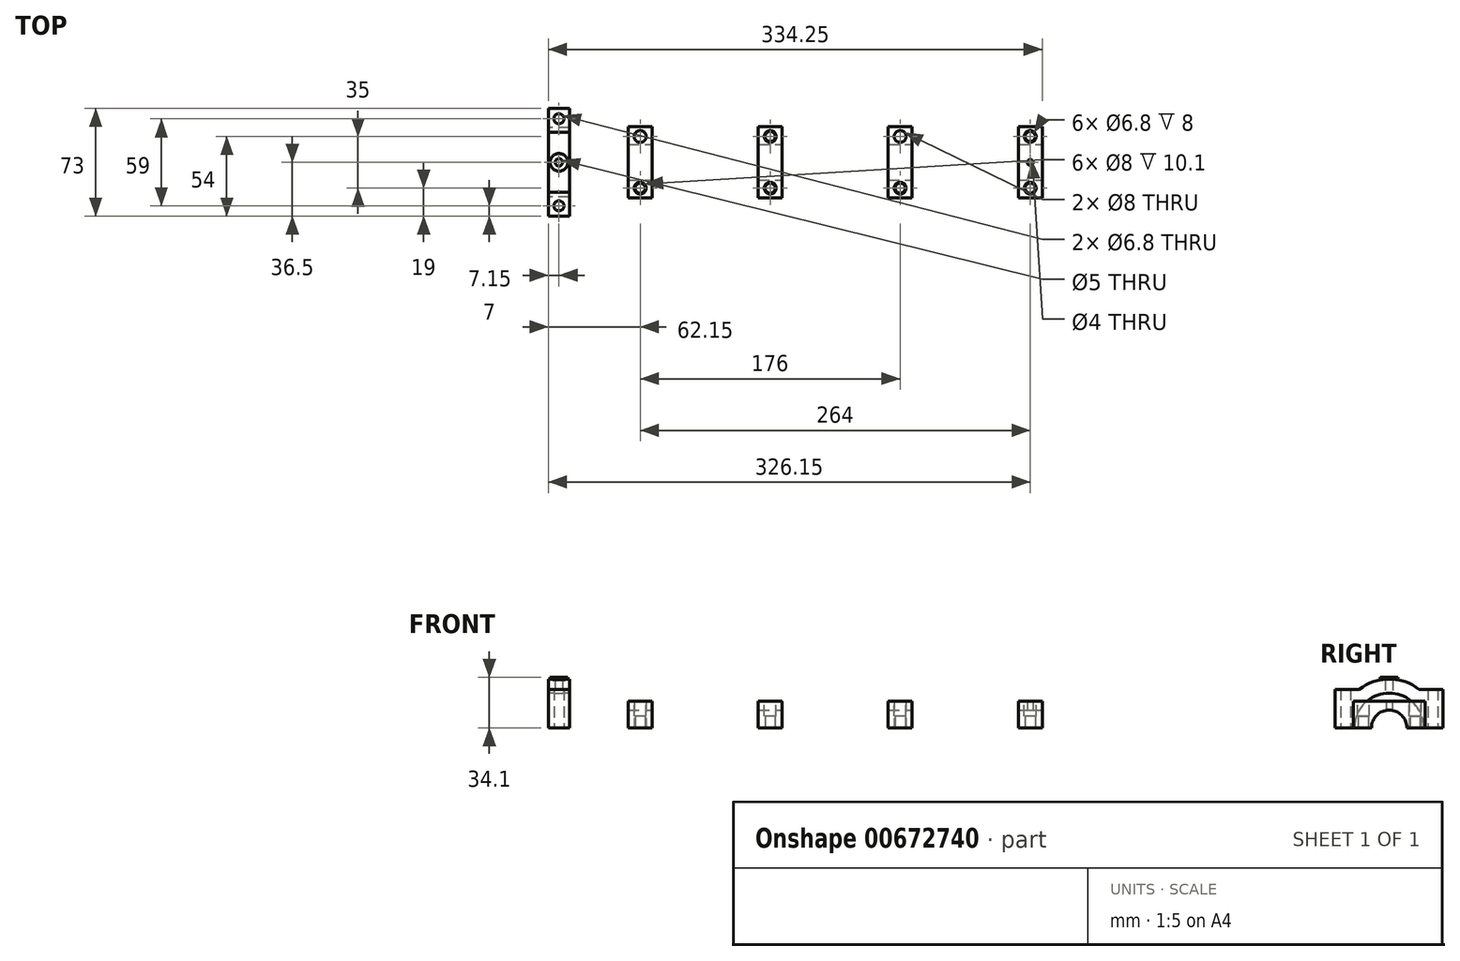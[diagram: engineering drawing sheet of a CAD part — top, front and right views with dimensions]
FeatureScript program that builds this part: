
annotation { "Feature Type Name" : "Feature", "Feature Type Description" : "" }
export const myFeature = defineFeature(function(context is Context, id is Id, definition is map)
    precondition{}
    {
        {
            var Q0;
            Q0=qCreatedBy(makeId("Top.planeOp"),FACE);
            var sketch = newSketch(context, id + "F0", { "sketchPlane" : qUnion([Q0])});
            skCircle(sketch, "E0", {"center": v(0, 0) * mm, "radius": 3.4 * mm});
            skCircle(sketch, "E1", {"center": v(55, -12) * mm, "radius": 4 * mm});
            skCircle(sketch, "E2", {"center": v(143, -12) * mm, "radius": 3.4 * mm});
            skCircle(sketch, "E3", {"center": v(319, -12) * mm, "radius": 3.4 * mm});
            skCircle(sketch, "E4", {"center": v(231, -12) * mm, "radius": 4 * mm});
            skCircle(sketch, "E5", {"center": v(231, -47) * mm, "radius": 3.4 * mm});
            skCircle(sketch, "E6", {"center": v(319, -47) * mm, "radius": 3.4 * mm});
            skCircle(sketch, "E7", {"center": v(143, -47) * mm, "radius": 3.4 * mm});
            skCircle(sketch, "E8", {"center": v(55, -47) * mm, "radius": 3.4 * mm});
            skCircle(sketch, "E9", {"center": v(0, -59) * mm, "radius": 3.4 * mm});
            skLineSegment(sketch, "E10", {"start": v(0, -29.5) * mm, "end": v(197.22, -29.5) * mm, "construction": true});
            skLineSegment(sketch, "E11", {"start": v(0, 0) * mm, "end": v(0, -59) * mm, "construction": true});
            skLineSegment(sketch, "E12", {"start": v(55, -12) * mm, "end": v(55, -47) * mm, "construction": true});
            skPoint(sketch, "E13", {"position": v(55, -29.5) * mm});
            skCircle(sketch, "E14", {"center": v(55, -12) * mm, "radius": 3.4 * mm});
            skCircle(sketch, "E15", {"center": v(231, -12) * mm, "radius": 3.4 * mm});
            skCircle(sketch, "E16", {"center": v(0, -29.5) * mm, "radius": 2.5 * mm});
            skCircle(sketch, "E17", {"center": v(27.5, -22) * mm, "radius": 3 * mm});
            skCircle(sketch, "E18", {"center": v(162.5, -22) * mm, "radius": 3 * mm});
            skCircle(sketch, "E19", {"center": v(298.5, -22) * mm, "radius": 3 * mm});
            skCircle(sketch, "E20", {"center": v(319, -29.5) * mm, "radius": 2 * mm});
            skLineSegment(sketch, "E21", {"start": v(55, 31.97) * mm, "end": v(55, -82.69) * mm, "construction": true});
            skLineSegment(sketch, "E22", {"start": v(143, 34.32) * mm, "end": v(143, -83.86) * mm, "construction": true});
            skLineSegment(sketch, "E23", {"start": v(231, 33.85) * mm, "end": v(231, -87.86) * mm, "construction": true});
            skLineSegment(sketch, "E24", {"start": v(319, 30.8) * mm, "end": v(319, -87.62) * mm, "construction": true});
            skLineSegment(sketch, "E25", {"start": v(0, 34.32) * mm, "end": v(0, -85.27) * mm, "construction": true});
            skSolve(sketch);
        }
        {
            var Q0;
            Q0=qCreatedBy(makeId("Top.planeOp"),FACE);
            var sketch = newSketch(context, id + "F1", { "sketchPlane" : qUnion([Q0])});
            skLineSegment(sketch, "E26", {"start": v(-7.15, 7) * mm, "end": v(-7.15, -66) * mm});
            skPoint(sketch, "E27", {"position": v(-7.15, -29.5) * mm});
            skLineSegment(sketch, "E28", {"start": v(-7.15, 7) * mm, "end": v(7.15, 7) * mm});
            skPoint(sketch, "E29", {"position": v(0, 7) * mm});
            skLineSegment(sketch, "E30", {"start": v(-7.15, -66) * mm, "end": v(7.15, -66) * mm});
            skLineSegment(sketch, "E31", {"start": v(7.15, -66) * mm, "end": v(7.15, -53.75) * mm});
            skLineSegment(sketch, "E32", {"start": v(7.15, -53.75) * mm, "end": v(327.1, -53.75) * mm});
            skLineSegment(sketch, "E33", {"start": v(327.1, -53.75) * mm, "end": v(327.1, -5.25) * mm});
            skLineSegment(sketch, "E34", {"start": v(327.1, -5.25) * mm, "end": v(7.15, -5.25) * mm});
            skLineSegment(sketch, "E35", {"start": v(7.15, -5.25) * mm, "end": v(7.15, 7) * mm});
            skPoint(sketch, "E36", {"position": v(327.1, -29.5) * mm});
            skSolve(sketch);
        }
        {
            var Q0;
            Q0 = qSketchRegion(id + "F1", true);
            extrude(context, id + "F2", {"entities" : qUnion([Q0]), "depth" : 39.1 * mm, "offsetDistance" : 25 * mm});
        }
        {
            var Q0;
            Q0=makeQuery(id+"F0.imprint","IMPRINT",FACE,{"disambiguationData":[TD([[makeQuery(id+"F0.imprint","IMPRINT",EDGE,{"derivedFrom":sQuery(id+"F0.wireOp",EDGE,"E1")}),1.0]])]});
            var Q1;
            Q1=makeQuery(id+"F0.imprint","IMPRINT",FACE,{"disambiguationData":[TD([[makeQuery(id+"F0.imprint","IMPRINT",EDGE,{"derivedFrom":sQuery(id+"F0.wireOp",EDGE,"E4")}),1.0]])]});
            extrude(context, id + "F3", {"entities" : qUnion([Q0, Q1]), "operationType" : NewBodyOperationType.REMOVE, "depth" : 11 * mm, "offsetDistance" : 25 * mm});
        }
        {
            var Q0;
            Q0=makeQuery(id+"F2.opExtrude","SWEPT_FACE",FACE,{"disambiguationData":[OSD([sQuery(id+"F1.wireOp",EDGE,"E33")])]});
            var sketch = newSketch(context, id + "F4", { "sketchPlane" : qUnion([Q0])});
            skCircle(sketch, "E37", {"center": v(-29.5, 0) * mm, "radius": 12 * mm});
            skSolve(sketch);
        }
        {
            var Q0;
            Q0 = qSketchRegion(id + "F4", true);
            var Q1;
            Q1=makeQuery(id+"F2.opExtrude","SWEPT_FACE",FACE,{"disambiguationData":[OSD([sQuery(id+"F1.wireOp",EDGE,"E26")])]});
            extrude(context, id + "F5", {"entities" : qUnion([Q0]), "operationType" : NewBodyOperationType.REMOVE, "endBound" : BoundingType.UP_TO_SURFACE, "oppositeDirection" : true, "depth" : 25 * mm, "endBoundEntityFace" : qUnion([Q1]), "offsetDistance" : 25 * mm});
        }
        {
            var Q0;
            Q0=makeQuery(id+"F2.opExtrude","SWEPT_FACE",FACE,{"disambiguationData":[OSD([sQuery(id+"F1.wireOp",EDGE,"E26")])]});
            var sketch = newSketch(context, id + "F6", { "sketchPlane" : qUnion([Q0])});
            skCircle(sketch, "E38", {"center": v(29.5, 0) * mm, "radius": 23.5 * mm});
            skSolve(sketch);
        }
        {
            var Q0;
            Q0 = qSketchRegion(id + "F6", true);
            var Q1;
            Q1=makeQuery(id+"F2.opExtrude","SWEPT_FACE",FACE,{"disambiguationData":[OSD([sQuery(id+"F1.wireOp",EDGE,"E31")])]});
            extrude(context, id + "F7", {"entities" : qUnion([Q0]), "operationType" : NewBodyOperationType.REMOVE, "oppositeDirection" : true, "depth" : 14.3 * mm, "endBoundEntityFace" : qUnion([Q1]), "offsetDistance" : 25 * mm});
        }
        {
            var Q0;
            Q0=qCreatedBy(makeId("Front.planeOp"),FACE);
            var sketch = newSketch(context, id + "F8", { "sketchPlane" : qUnion([Q0])});
            skLineSegment(sketch, "E39", {"start": v(7.15, 0) * mm, "end": v(7.15, 15.3) * mm});
            skLineSegment(sketch, "E40", {"start": v(7.15, 15.3) * mm, "end": v(46.85, 15.3) * mm});
            skLineSegment(sketch, "E41", {"start": v(46.85, 15.3) * mm, "end": v(46.85, 0) * mm});
            skLineSegment(sketch, "E42", {"start": v(46.85, 0) * mm, "end": v(63.15, 0) * mm});
            skLineSegment(sketch, "E43", {"start": v(63.15, 0) * mm, "end": v(63.15, 15.3) * mm});
            skLineSegment(sketch, "E44", {"start": v(63.15, 15.3) * mm, "end": v(134.85, 15.3) * mm});
            skLineSegment(sketch, "E45", {"start": v(134.85, 15.3) * mm, "end": v(134.85, 0) * mm});
            skLineSegment(sketch, "E46", {"start": v(134.85, 0) * mm, "end": v(151.15, 0) * mm});
            skLineSegment(sketch, "E47", {"start": v(151.15, 0) * mm, "end": v(151.15, 15.3) * mm});
            skLineSegment(sketch, "E48", {"start": v(151.15, 15.3) * mm, "end": v(222.85, 15.3) * mm});
            skLineSegment(sketch, "E49", {"start": v(222.85, 15.3) * mm, "end": v(222.85, 0) * mm});
            skLineSegment(sketch, "E50", {"start": v(222.85, 0) * mm, "end": v(239.15, 0) * mm});
            skLineSegment(sketch, "E51", {"start": v(239.15, 0) * mm, "end": v(239.15, 15.3) * mm});
            skLineSegment(sketch, "E52", {"start": v(239.15, 15.3) * mm, "end": v(310.9, 15.3) * mm});
            skLineSegment(sketch, "E53", {"start": v(310.9, 15.3) * mm, "end": v(310.9, 0) * mm});
            skLineSegment(sketch, "E54", {"start": v(310.9, 0) * mm, "end": v(327.1, 0) * mm});
            skLineSegment(sketch, "E55", {"start": v(327.1, 0) * mm, "end": v(327.1, 15.3) * mm});
            skLineSegment(sketch, "E56", {"start": v(7.15, 0) * mm, "end": v(310.9, 0) * mm});
            skPoint(sketch, "E57", {"position": v(55, 0) * mm});
            skPoint(sketch, "E58", {"position": v(143, 0) * mm});
            skPoint(sketch, "E59", {"position": v(231, 0) * mm});
            skPoint(sketch, "E60", {"position": v(319, 0) * mm});
            skSolve(sketch);
        }
        {
            var Q0;
            {var subQ0=sQuery(id+"F8.wireOp",EDGE,"E39");Q0=makeQuery(id+"F8.imprint","IMPRINT",FACE,{"disambiguationData":[TD([[makeQuery(id+"F8.imprint","IMPRINT",EDGE,{"derivedFrom":subQ0}),-1.0]])]});}
            var Q1;
            {var subQ0=sQuery(id+"F8.wireOp",EDGE,"E43");Q1=makeQuery(id+"F8.imprint","IMPRINT",FACE,{"disambiguationData":[TD([[makeQuery(id+"F8.imprint","IMPRINT",EDGE,{"derivedFrom":subQ0}),-1.0]])]});}
            var Q2;
            {var subQ0=sQuery(id+"F8.wireOp",EDGE,"E47");Q2=makeQuery(id+"F8.imprint","IMPRINT",FACE,{"disambiguationData":[TD([[makeQuery(id+"F8.imprint","IMPRINT",EDGE,{"derivedFrom":subQ0}),-1.0]])]});}
            var Q3;
            {var subQ0=sQuery(id+"F8.wireOp",EDGE,"E51");Q3=makeQuery(id+"F8.imprint","IMPRINT",FACE,{"disambiguationData":[TD([[makeQuery(id+"F8.imprint","IMPRINT",EDGE,{"derivedFrom":subQ0}),-1.0]])]});}
            var Q4;
            Q4=makeQuery(id+"F2.opExtrude","SWEPT_FACE",FACE,{"disambiguationData":[OSD([sQuery(id+"F1.wireOp",EDGE,"E32")])]});
            extrude(context, id + "F9", {"entities" : qUnion([Q0, Q1, Q2, Q3]), "operationType" : NewBodyOperationType.REMOVE, "endBound" : BoundingType.UP_TO_SURFACE, "depth" : 25 * mm, "endBoundEntityFace" : qUnion([Q4]), "offsetDistance" : 25 * mm});
        }
        {
            var Q0;
            Q0=makeQuery(id+"F9.boolean.opBoolean","MERGE",FACE,{"derivedFrom":[makeQuery(id+"F2.opExtrude","SWEPT_FACE",FACE,{"disambiguationData":[OSD([sQuery(id+"F1.wireOp",EDGE,"E31")])]}),makeQuery(id+"F9.opExtrude","SWEPT_FACE",FACE,{"disambiguationData":[OSD([sQuery(id+"F8.wireOp",EDGE,"E39")])]})]});
            cPlane(context, id + "F10", {"entities" : qUnion([Q0]), "cplaneType" : CPlaneType.OFFSET, "offset" : 0 * mm, "width" : 150 * mm, "height" : 150 * mm});
        }
        {
            var Q0;
            Q0=makeQuery(id+"F9.boolean.opBoolean","COPY",FACE,{"derivedFrom":makeQuery(id+"F9.opExtrude","SWEPT_FACE",FACE,{"disambiguationData":[OSD([sQuery(id+"F8.wireOp",EDGE,"E43")])]})});
            cPlane(context, id + "F11", {"entities" : qUnion([Q0]), "cplaneType" : CPlaneType.OFFSET, "offset" : 0 * mm, "width" : 150 * mm, "height" : 150 * mm});
        }
        {
            var Q0;
            Q0=makeQuery(id+"F9.boolean.opBoolean","COPY",FACE,{"derivedFrom":makeQuery(id+"F9.opExtrude","SWEPT_FACE",FACE,{"disambiguationData":[OSD([sQuery(id+"F8.wireOp",EDGE,"E47")])]})});
            cPlane(context, id + "F12", {"entities" : qUnion([Q0]), "cplaneType" : CPlaneType.OFFSET, "offset" : 0 * mm, "width" : 150 * mm, "height" : 150 * mm});
        }
        {
            var Q0;
            Q0=makeQuery(id+"F9.boolean.opBoolean","COPY",FACE,{"derivedFrom":makeQuery(id+"F9.opExtrude","SWEPT_FACE",FACE,{"disambiguationData":[OSD([sQuery(id+"F8.wireOp",EDGE,"E51")])]})});
            cPlane(context, id + "F13", {"entities" : qUnion([Q0]), "cplaneType" : CPlaneType.OFFSET, "offset" : 0 * mm, "width" : 150 * mm, "height" : 150 * mm});
        }
        {
            var Q0;
            Q0=makeQuery(id+"F2.opExtrude","CAP_FACE",FACE,{"disambiguationData":[OSD([sQuery(id+"F1.wireOp",EDGE,"E26"),sQuery(id+"F1.wireOp",EDGE,"E28"),sQuery(id+"F1.wireOp",EDGE,"E30"),sQuery(id+"F1.wireOp",EDGE,"E31"),sQuery(id+"F1.wireOp",EDGE,"E32"),sQuery(id+"F1.wireOp",EDGE,"E33"),sQuery(id+"F1.wireOp",EDGE,"E34"),sQuery(id+"F1.wireOp",EDGE,"E35")])],"isStart":false});
            cPlane(context, id + "F14", {"entities" : qUnion([Q0]), "cplaneType" : CPlaneType.OFFSET, "offset" : 0 * mm, "width" : 150 * mm, "height" : 150 * mm});
        }
        {
            var Q0;
            Q0=qCreatedBy(id+"F14.planeOp",FACE);
            var sketch = newSketch(context, id + "F15", { "sketchPlane" : qUnion([Q0])});
            skCircle(sketch, "E61", {"center": v(298.5, -22) * mm, "radius": 6.5 * mm});
            skCircle(sketch, "E62", {"center": v(162.5, -22) * mm, "radius": 6.5 * mm});
            skCircle(sketch, "E63", {"center": v(27.5, -22) * mm, "radius": 6.5 * mm});
            skCircle(sketch, "E64", {"center": v(0, -29.5) * mm, "radius": 6 * mm});
            skSolve(sketch);
        }
        {
            var Q0;
            Q0=qCreatedBy(id+"F10.planeOp",FACE);
            var sketch = newSketch(context, id + "F16", { "sketchPlane" : qUnion([Q0])});
            skCircle(sketch, "E65", {"center": v(-29.5, 0) * mm, "radius": 24.75 * mm});
            skSolve(sketch);
        }
        {
            var Q0;
            Q0=qCreatedBy(id+"F11.planeOp",FACE);
            var sketch = newSketch(context, id + "F17", { "sketchPlane" : qUnion([Q0])});
            skCircle(sketch, "E66", {"center": v(-29.5, 0) * mm, "radius": 25 * mm});
            skSolve(sketch);
        }
        {
            var Q0;
            Q0=qCreatedBy(id+"F12.planeOp",FACE);
            var sketch = newSketch(context, id + "F18", { "sketchPlane" : qUnion([Q0])});
            skCircle(sketch, "E67", {"center": v(-29.5, 0) * mm, "radius": 25 * mm});
            skSolve(sketch);
        }
        {
            var Q0;
            Q0=qCreatedBy(id+"F13.planeOp",FACE);
            var sketch = newSketch(context, id + "F19", { "sketchPlane" : qUnion([Q0])});
            skCircle(sketch, "E68", {"center": v(-29.5, 0) * mm, "radius": 25 * mm});
            skSolve(sketch);
        }
        {
            var Q0;
            Q0=makeQuery(id+"F2.opExtrude","SWEPT_FACE",FACE,{"disambiguationData":[OSD([sQuery(id+"F1.wireOp",EDGE,"E26")])]});
            cPlane(context, id + "F20", {"entities" : qUnion([Q0]), "cplaneType" : CPlaneType.OFFSET, "offset" : 0 * mm, "width" : 150 * mm, "height" : 150 * mm});
        }
        {
            var Q0;
            Q0=qCreatedBy(id+"F20.planeOp",FACE);
            var sketch = newSketch(context, id + "F21", { "sketchPlane" : qUnion([Q0])});
            skArc(sketch, "E69", {"start": v(49.82, 26) * mm, "mid": v(29.5, 33) * mm, "end": v(9.18, 26) * mm});
            skLineSegment(sketch, "E70", {"start": v(-7, 26) * mm, "end": v(9.18, 26) * mm});
            skLineSegment(sketch, "E71", {"start": v(49.82, 26) * mm, "end": v(66, 26) * mm});
            skLineSegment(sketch, "E72", {"start": v(-7, 26) * mm, "end": v(-7, 39.1) * mm});
            skLineSegment(sketch, "E73", {"start": v(-7, 39.1) * mm, "end": v(66, 39.1) * mm});
            skLineSegment(sketch, "E74", {"start": v(66, 39.1) * mm, "end": v(66, 26) * mm});
            skSolve(sketch);
        }
        {
            var Q0;
            Q0 = qSketchRegion(id + "F21", true);
            var Q1;
            {var subQ0=sQuery(id+"F16.wireOp",EDGE,"E65");var subQ1=sQuery(id+"F8.wireOp",EDGE,"E39");var subQ2=sQuery(id+"F1.wireOp",EDGE,"E35");var subQ3=sQuery(id+"F1.wireOp",EDGE,"E31");var subQ4=makeQuery(id+"F9.opExtrude","SWEPT_FACE",FACE,{"disambiguationData":[OSD([subQ1])]});Q1=makeQuery(id+"F31.boolean.opBoolean","MERGE",FACE,{"derivedFrom":[makeQuery(id+"F23.boolean.opBoolean","MERGE",FACE,{"derivedFrom":[makeQuery(id+"F9.boolean.opBoolean","MERGE",FACE,{"derivedFrom":[makeQuery(id+"F2.opExtrude","SWEPT_FACE",FACE,{"disambiguationData":[OSD([subQ3])]}),subQ4]}),makeQuery(id+"F9.boolean.opBoolean","MERGE",FACE,{"derivedFrom":[makeQuery(id+"F2.opExtrude","SWEPT_FACE",FACE,{"disambiguationData":[OSD([subQ2])]}),subQ4]}),makeQuery(id+"F23.opExtrude","CAP_FACE",FACE,{"disambiguationData":[OSD([subQ0])],"isStart":true})]}),makeQuery(id+"F31.opExtrude","CAP_FACE",FACE,{"disambiguationData":[OSD([subQ3,subQ2,subQ1,subQ0])],"isStart":false})]});}
            extrude(context, id + "F22", {"entities" : qUnion([Q0]), "operationType" : NewBodyOperationType.REMOVE, "endBound" : BoundingType.UP_TO_SURFACE, "oppositeDirection" : true, "depth" : 25 * mm, "endBoundEntityFace" : qUnion([Q1]), "offsetDistance" : 25 * mm});
        }
        {
            var Q0;
            Q0=makeQuery(id+"F16.imprint","IMPRINT",FACE,{"disambiguationData":[TD([[makeQuery(id+"F16.imprint","IMPRINT",EDGE,{"derivedFrom":sQuery(id+"F16.wireOp",EDGE,"E65")}),1.0]])]});
            var Q1;
            Q1=makeQuery(id+"F9.boolean.opBoolean","COPY",FACE,{"derivedFrom":makeQuery(id+"F9.opExtrude","SWEPT_FACE",FACE,{"disambiguationData":[OSD([sQuery(id+"F8.wireOp",EDGE,"E41")])]})});
            extrude(context, id + "F23", {"entities" : qUnion([Q0]), "operationType" : NewBodyOperationType.REMOVE, "endBound" : BoundingType.UP_TO_SURFACE, "depth" : 25 * mm, "endBoundEntityFace" : qUnion([Q1]), "offsetDistance" : 25 * mm});
        }
        {
            var Q0;
            Q0=makeQuery(id+"F17.imprint","IMPRINT",FACE,{"disambiguationData":[TD([[makeQuery(id+"F17.imprint","IMPRINT",EDGE,{"derivedFrom":sQuery(id+"F17.wireOp",EDGE,"E66")}),1.0]])]});
            var Q1;
            Q1=makeQuery(id+"F9.boolean.opBoolean","COPY",FACE,{"derivedFrom":makeQuery(id+"F9.opExtrude","SWEPT_FACE",FACE,{"disambiguationData":[OSD([sQuery(id+"F8.wireOp",EDGE,"E45")])]})});
            extrude(context, id + "F24", {"entities" : qUnion([Q0]), "operationType" : NewBodyOperationType.REMOVE, "endBound" : BoundingType.UP_TO_SURFACE, "depth" : 25 * mm, "endBoundEntityFace" : qUnion([Q1]), "offsetDistance" : 25 * mm});
        }
        {
            var Q0;
            Q0=makeQuery(id+"F18.imprint","IMPRINT",FACE,{"disambiguationData":[TD([[makeQuery(id+"F18.imprint","IMPRINT",EDGE,{"derivedFrom":sQuery(id+"F18.wireOp",EDGE,"E67")}),1.0]])]});
            var Q1;
            Q1=makeQuery(id+"F9.boolean.opBoolean","COPY",FACE,{"derivedFrom":makeQuery(id+"F9.opExtrude","SWEPT_FACE",FACE,{"disambiguationData":[OSD([sQuery(id+"F8.wireOp",EDGE,"E49")])]})});
            extrude(context, id + "F25", {"entities" : qUnion([Q0]), "operationType" : NewBodyOperationType.REMOVE, "endBound" : BoundingType.UP_TO_SURFACE, "depth" : 25 * mm, "endBoundEntityFace" : qUnion([Q1]), "offsetDistance" : 25 * mm});
        }
        {
            var Q0;
            Q0=makeQuery(id+"F19.imprint","IMPRINT",FACE,{"disambiguationData":[TD([[makeQuery(id+"F19.imprint","IMPRINT",EDGE,{"derivedFrom":sQuery(id+"F19.wireOp",EDGE,"E68")}),1.0]])]});
            var Q1;
            Q1=makeQuery(id+"F9.boolean.opBoolean","COPY",FACE,{"derivedFrom":makeQuery(id+"F9.opExtrude","SWEPT_FACE",FACE,{"disambiguationData":[OSD([sQuery(id+"F8.wireOp",EDGE,"E53")])]})});
            extrude(context, id + "F26", {"entities" : qUnion([Q0]), "operationType" : NewBodyOperationType.REMOVE, "endBound" : BoundingType.UP_TO_SURFACE, "depth" : 25 * mm, "endBoundEntityFace" : qUnion([Q1]), "offsetDistance" : 25 * mm});
        }
        {
            var Q0;
            Q0=makeQuery(id+"F2.opExtrude","CAP_FACE",FACE,{"disambiguationData":[OSD([sQuery(id+"F1.wireOp",EDGE,"E26"),sQuery(id+"F1.wireOp",EDGE,"E28"),sQuery(id+"F1.wireOp",EDGE,"E30"),sQuery(id+"F1.wireOp",EDGE,"E31"),sQuery(id+"F1.wireOp",EDGE,"E32"),sQuery(id+"F1.wireOp",EDGE,"E33"),sQuery(id+"F1.wireOp",EDGE,"E34"),sQuery(id+"F1.wireOp",EDGE,"E35")])],"isStart":false});
            var sketch = newSketch(context, id + "F27", { "sketchPlane" : qUnion([Q0])});
            skArc(sketch, "E75", {"start": v(327.1, -47) * mm, "mid": v(319, -38.9) * mm, "end": v(310.9, -47) * mm});
            skLineSegment(sketch, "E76", {"start": v(310.9, -47) * mm, "end": v(310.9, -59) * mm});
            skLineSegment(sketch, "E77", {"start": v(310.9, -59) * mm, "end": v(327.1, -59) * mm});
            skLineSegment(sketch, "E78", {"start": v(327.1, -59) * mm, "end": v(327.1, -47) * mm});
            skArc(sketch, "E79", {"start": v(239.1, -47) * mm, "mid": v(231, -38.9) * mm, "end": v(222.9, -47) * mm});
            skLineSegment(sketch, "E80", {"start": v(222.9, -47) * mm, "end": v(222.9, -59) * mm});
            skLineSegment(sketch, "E81", {"start": v(222.9, -59) * mm, "end": v(239.1, -59) * mm});
            skLineSegment(sketch, "E82", {"start": v(239.1, -59) * mm, "end": v(239.1, -47) * mm});
            skArc(sketch, "E83", {"start": v(151.1, -47) * mm, "mid": v(143, -38.9) * mm, "end": v(134.9, -47) * mm});
            skLineSegment(sketch, "E84", {"start": v(134.9, -47) * mm, "end": v(134.9, -59) * mm});
            skLineSegment(sketch, "E85", {"start": v(134.9, -59) * mm, "end": v(151.1, -59) * mm});
            skLineSegment(sketch, "E86", {"start": v(151.1, -59) * mm, "end": v(151.1, -47) * mm});
            skArc(sketch, "E87", {"start": v(63.1, -47) * mm, "mid": v(55, -38.9) * mm, "end": v(46.9, -47) * mm});
            skLineSegment(sketch, "E88", {"start": v(46.9, -47) * mm, "end": v(46.9, -59) * mm});
            skLineSegment(sketch, "E89", {"start": v(46.9, -59) * mm, "end": v(63.1, -59) * mm});
            skLineSegment(sketch, "E90", {"start": v(63.1, -59) * mm, "end": v(63.1, -47) * mm});
            skLineSegment(sketch, "E91", {"start": v(-23.17, -29.5) * mm, "end": v(371.55, -29.5) * mm, "construction": true});
            skArc(sketch, "E92.MirrorC", {"start": v(327.1, -12) * mm, "mid": v(319, -20.1) * mm, "end": v(310.9, -12) * mm});
            skLineSegment(sketch, "E93.MirrorCS", {"start": v(63.1, 0) * mm, "end": v(63.1, -12) * mm});
            skLineSegment(sketch, "E94.MirrorCS", {"start": v(46.9, 0) * mm, "end": v(63.1, 0) * mm});
            skLineSegment(sketch, "E95.MirrorCS", {"start": v(46.9, -12) * mm, "end": v(46.9, 0) * mm});
            skLineSegment(sketch, "E96.MirrorCS", {"start": v(239.1, 0) * mm, "end": v(239.1, -12) * mm});
            skArc(sketch, "E97.MirrorC", {"start": v(63.1, -12) * mm, "mid": v(55, -20.1) * mm, "end": v(46.9, -12) * mm});
            skLineSegment(sketch, "E98.MirrorCS", {"start": v(151.1, 0) * mm, "end": v(151.1, -12) * mm});
            skArc(sketch, "E99.MirrorC", {"start": v(151.1, -12) * mm, "mid": v(143, -20.1) * mm, "end": v(134.9, -12) * mm});
            skLineSegment(sketch, "E100.MirrorCS", {"start": v(310.9, -12) * mm, "end": v(310.9, 0) * mm});
            skLineSegment(sketch, "E101.MirrorCS", {"start": v(134.9, -12) * mm, "end": v(134.9, 0) * mm});
            skLineSegment(sketch, "E102.MirrorCS", {"start": v(222.9, -12) * mm, "end": v(222.9, 0) * mm});
            skLineSegment(sketch, "E103.MirrorCS", {"start": v(222.9, 0) * mm, "end": v(239.1, 0) * mm});
            skArc(sketch, "E104.MirrorC", {"start": v(239.1, -12) * mm, "mid": v(231, -20.1) * mm, "end": v(222.9, -12) * mm});
            skLineSegment(sketch, "E105.MirrorCS", {"start": v(327.1, 0) * mm, "end": v(327.1, -12) * mm});
            skLineSegment(sketch, "E106.MirrorCS", {"start": v(134.9, 0) * mm, "end": v(151.1, 0) * mm});
            skLineSegment(sketch, "E107.MirrorCS", {"start": v(310.9, 0) * mm, "end": v(327.1, 0) * mm});
            skSolve(sketch);
        }
        {
            var Q0;
            {var subQ2=sQuery(id+"F27.wireOp",EDGE,"E87");Q0=makeQuery(id+"F27.imprint","IMPRINT",FACE,{"disambiguationData":[TD([[makeQuery(id+"F27.imprint","IMPRINT",EDGE,{"derivedFrom":subQ2}),1.0]])]});}
            var Q1;
            {var subQ1=sQuery(id+"F27.wireOp",EDGE,"E97.MirrorC");Q1=makeQuery(id+"F27.imprint","IMPRINT",FACE,{"disambiguationData":[TD([[makeQuery(id+"F27.imprint","IMPRINT",EDGE,{"derivedFrom":subQ1}),-1.0]])]});}
            var Q2;
            {var subQ1=sQuery(id+"F27.wireOp",EDGE,"E99.MirrorC");Q2=makeQuery(id+"F27.imprint","IMPRINT",FACE,{"disambiguationData":[TD([[makeQuery(id+"F27.imprint","IMPRINT",EDGE,{"derivedFrom":subQ1}),-1.0]])]});}
            var Q3;
            {var subQ2=sQuery(id+"F27.wireOp",EDGE,"E83");Q3=makeQuery(id+"F27.imprint","IMPRINT",FACE,{"disambiguationData":[TD([[makeQuery(id+"F27.imprint","IMPRINT",EDGE,{"derivedFrom":subQ2}),1.0]])]});}
            var Q4;
            {var subQ1=sQuery(id+"F27.wireOp",EDGE,"E104.MirrorC");Q4=makeQuery(id+"F27.imprint","IMPRINT",FACE,{"disambiguationData":[TD([[makeQuery(id+"F27.imprint","IMPRINT",EDGE,{"derivedFrom":subQ1}),-1.0]])]});}
            var Q5;
            {var subQ2=sQuery(id+"F27.wireOp",EDGE,"E79");Q5=makeQuery(id+"F27.imprint","IMPRINT",FACE,{"disambiguationData":[TD([[makeQuery(id+"F27.imprint","IMPRINT",EDGE,{"derivedFrom":subQ2}),1.0]])]});}
            var Q6;
            {var subQ4=sQuery(id+"F27.wireOp",EDGE,"E92.MirrorC");Q6=makeQuery(id+"F27.imprint","IMPRINT",FACE,{"disambiguationData":[TD([[makeQuery(id+"F27.imprint","IMPRINT",EDGE,{"derivedFrom":subQ4}),-1.0]])]});}
            var Q7;
            {var subQ7=sQuery(id+"F27.wireOp",EDGE,"E75");Q7=makeQuery(id+"F27.imprint","IMPRINT",FACE,{"disambiguationData":[TD([[makeQuery(id+"F27.imprint","IMPRINT",EDGE,{"derivedFrom":subQ7}),1.0]])]});}
            extrude(context, id + "F28", {"entities" : qUnion([Q0, Q1, Q2, Q3, Q4, Q5, Q6, Q7]), "operationType" : NewBodyOperationType.REMOVE, "oppositeDirection" : true, "depth" : 18 * mm, "offsetDistance" : 25 * mm});
        }
        {
            var Q0;
            Q0=makeQuery(id+"F2.opExtrude","SWEPT_FACE",FACE,{"disambiguationData":[OSD([sQuery(id+"F1.wireOp",EDGE,"E33")])]});
            cPlane(context, id + "F29", {"entities" : qUnion([Q0]), "cplaneType" : CPlaneType.OFFSET, "offset" : 0 * mm, "width" : 150 * mm, "height" : 150 * mm});
        }
        {
            var Q0;
            Q0=qCreatedBy(id+"F29.planeOp",FACE);
            var sketch = newSketch(context, id + "F30", { "sketchPlane" : qUnion([Q0])});
            skCircle(sketch, "E108", {"center": v(-29.5, 0) * mm, "radius": 30.8 * mm});
            skCircle(sketch, "E109", {"center": v(-29.5, 0) * mm, "radius": 50 * mm});
            skSolve(sketch);
        }
        {
            var Q0;
            Q0=makeQuery(id+"F30.imprint","IMPRINT",FACE,{"disambiguationData":[TD([[makeQuery(id+"F30.imprint","IMPRINT",EDGE,{"derivedFrom":sQuery(id+"F30.wireOp",EDGE,"E108")}),-1.0]])]});
            var Q1;
            {var subQ0=makeQuery(id+"F9.opExtrude","SWEPT_FACE",FACE,{"disambiguationData":[OSD([sQuery(id+"F8.wireOp",EDGE,"E39")])]});Q1=makeQuery(id+"F23.boolean.opBoolean","MERGE",FACE,{"derivedFrom":[makeQuery(id+"F9.boolean.opBoolean","MERGE",FACE,{"derivedFrom":[makeQuery(id+"F2.opExtrude","SWEPT_FACE",FACE,{"disambiguationData":[OSD([sQuery(id+"F1.wireOp",EDGE,"E31")])]}),subQ0]}),makeQuery(id+"F9.boolean.opBoolean","MERGE",FACE,{"derivedFrom":[makeQuery(id+"F2.opExtrude","SWEPT_FACE",FACE,{"disambiguationData":[OSD([sQuery(id+"F1.wireOp",EDGE,"E35")])]}),subQ0]}),makeQuery(id+"F23.opExtrude","CAP_FACE",FACE,{"disambiguationData":[OSD([sQuery(id+"F16.wireOp",EDGE,"E65")])],"isStart":true})]});}
            extrude(context, id + "F31", {"entities" : qUnion([Q0]), "operationType" : NewBodyOperationType.REMOVE, "endBound" : BoundingType.UP_TO_SURFACE, "oppositeDirection" : true, "depth" : 287.2 * mm, "endBoundEntityFace" : qUnion([Q1]), "offsetDistance" : 25 * mm});
        }
        {
            var Q0;
            Q0=makeQuery(id+"F15.imprint","IMPRINT",FACE,{"disambiguationData":[TD([[makeQuery(id+"F15.imprint","IMPRINT",EDGE,{"derivedFrom":sQuery(id+"F15.wireOp",EDGE,"E63")}),1.0]])]});
            var Q1;
            Q1=makeQuery(id+"F15.imprint","IMPRINT",FACE,{"disambiguationData":[TD([[makeQuery(id+"F15.imprint","IMPRINT",EDGE,{"derivedFrom":sQuery(id+"F15.wireOp",EDGE,"E62")}),1.0]])]});
            var Q2;
            Q2=makeQuery(id+"F15.imprint","IMPRINT",FACE,{"disambiguationData":[TD([[makeQuery(id+"F15.imprint","IMPRINT",EDGE,{"derivedFrom":sQuery(id+"F15.wireOp",EDGE,"E61")}),1.0]])]});
            var Q3;
            Q3=makeQuery(id+"F15.imprint","IMPRINT",FACE,{"disambiguationData":[TD([[makeQuery(id+"F15.imprint","IMPRINT",EDGE,{"derivedFrom":sQuery(id+"F15.wireOp",EDGE,"E64")}),1.0]])]});
            var Q4;
            Q4=makeQuery(id+"F31.boolean.opBoolean","COPY",FACE,{"derivedFrom":makeQuery(id+"F31.opExtrude","SWEPT_FACE",FACE,{"disambiguationData":[OSD([sQuery(id+"F30.wireOp",EDGE,"E108")])]})});
            extrude(context, id + "F32", {"entities" : qUnion([Q0, Q1, Q2, Q3]), "operationType" : NewBodyOperationType.ADD, "endBound" : BoundingType.UP_TO_SURFACE, "oppositeDirection" : true, "depth" : 25 * mm, "endBoundEntityFace" : qUnion([Q4]), "offsetDistance" : 25 * mm});
        }
        {
            var Q0;
            Q0=makeQuery(id+"F0.imprint","IMPRINT",FACE,{"disambiguationData":[TD([[makeQuery(id+"F0.imprint","IMPRINT",EDGE,{"derivedFrom":sQuery(id+"F0.wireOp",EDGE,"E0")}),1.0]])]});
            var Q1;
            Q1=makeQuery(id+"F0.imprint","IMPRINT",FACE,{"disambiguationData":[TD([[makeQuery(id+"F0.imprint","IMPRINT",EDGE,{"derivedFrom":sQuery(id+"F0.wireOp",EDGE,"E2")}),1.0]])]});
            var Q2;
            Q2=makeQuery(id+"F0.imprint","IMPRINT",FACE,{"disambiguationData":[TD([[makeQuery(id+"F0.imprint","IMPRINT",EDGE,{"derivedFrom":sQuery(id+"F0.wireOp",EDGE,"E3")}),1.0]])]});
            var Q3;
            Q3=makeQuery(id+"F0.imprint","IMPRINT",FACE,{"disambiguationData":[TD([[makeQuery(id+"F0.imprint","IMPRINT",EDGE,{"derivedFrom":sQuery(id+"F0.wireOp",EDGE,"E5")}),1.0]])]});
            var Q4;
            Q4=makeQuery(id+"F0.imprint","IMPRINT",FACE,{"disambiguationData":[TD([[makeQuery(id+"F0.imprint","IMPRINT",EDGE,{"derivedFrom":sQuery(id+"F0.wireOp",EDGE,"E6")}),1.0]])]});
            var Q5;
            Q5=makeQuery(id+"F0.imprint","IMPRINT",FACE,{"disambiguationData":[TD([[makeQuery(id+"F0.imprint","IMPRINT",EDGE,{"derivedFrom":sQuery(id+"F0.wireOp",EDGE,"E7")}),1.0]])]});
            var Q6;
            Q6=makeQuery(id+"F0.imprint","IMPRINT",FACE,{"disambiguationData":[TD([[makeQuery(id+"F0.imprint","IMPRINT",EDGE,{"derivedFrom":sQuery(id+"F0.wireOp",EDGE,"E8")}),1.0]])]});
            var Q7;
            Q7=makeQuery(id+"F0.imprint","IMPRINT",FACE,{"disambiguationData":[TD([[makeQuery(id+"F0.imprint","IMPRINT",EDGE,{"derivedFrom":sQuery(id+"F0.wireOp",EDGE,"E9")}),1.0]])]});
            var Q8;
            Q8=makeQuery(id+"F0.imprint","IMPRINT",FACE,{"disambiguationData":[TD([[makeQuery(id+"F0.imprint","IMPRINT",EDGE,{"derivedFrom":sQuery(id+"F0.wireOp",EDGE,"E16")}),1.0]])]});
            var Q9;
            Q9=makeQuery(id+"F0.imprint","IMPRINT",FACE,{"disambiguationData":[TD([[makeQuery(id+"F0.imprint","IMPRINT",EDGE,{"derivedFrom":sQuery(id+"F0.wireOp",EDGE,"E17")}),1.0]])]});
            var Q10;
            Q10=makeQuery(id+"F0.imprint","IMPRINT",FACE,{"disambiguationData":[TD([[makeQuery(id+"F0.imprint","IMPRINT",EDGE,{"derivedFrom":sQuery(id+"F0.wireOp",EDGE,"E18")}),1.0]])]});
            var Q11;
            Q11=makeQuery(id+"F0.imprint","IMPRINT",FACE,{"disambiguationData":[TD([[makeQuery(id+"F0.imprint","IMPRINT",EDGE,{"derivedFrom":sQuery(id+"F0.wireOp",EDGE,"E19")}),1.0]])]});
            var Q12;
            Q12=makeQuery(id+"F0.imprint","IMPRINT",FACE,{"disambiguationData":[TD([[makeQuery(id+"F0.imprint","IMPRINT",EDGE,{"derivedFrom":sQuery(id+"F0.wireOp",EDGE,"E14")}),1.0]])]});
            var Q13;
            Q13=makeQuery(id+"F0.imprint","IMPRINT",FACE,{"disambiguationData":[TD([[makeQuery(id+"F0.imprint","IMPRINT",EDGE,{"derivedFrom":sQuery(id+"F0.wireOp",EDGE,"E15")}),1.0]])]});
            var Q14;
            Q14=makeQuery(id+"F0.imprint","IMPRINT",FACE,{"disambiguationData":[TD([[makeQuery(id+"F0.imprint","IMPRINT",EDGE,{"derivedFrom":sQuery(id+"F0.wireOp",EDGE,"E20")}),1.0]])]});
            extrude(context, id + "F33", {"entities" : qUnion([Q0, Q1, Q2, Q3, Q4, Q5, Q6, Q7, Q8, Q9, Q10, Q11, Q12, Q13, Q14]), "operationType" : NewBodyOperationType.REMOVE, "endBound" : BoundingType.THROUGH_ALL, "depth" : 25 * mm, "offsetDistance" : 25 * mm});
        }
        {
            var Q0;
            Q0=qCreatedBy(id+"F29.planeOp",FACE);
            var sketch = newSketch(context, id + "F34", { "sketchPlane" : qUnion([Q0])});
            skArc(sketch, "E110", {"start": v(-9.7, 27.4) * mm, "mid": v(-29.5, 33.8) * mm, "end": v(-49.3, 27.4) * mm});
            skLineSegment(sketch, "E111", {"start": v(-49.3, 27.4) * mm, "end": v(-66.68, 27.4) * mm});
            skLineSegment(sketch, "E112", {"start": v(-9.7, 27.4) * mm, "end": v(-0.46, 27.4) * mm});
            skLineSegment(sketch, "E113", {"start": v(-66.68, 27.4) * mm, "end": v(-66.68, 30.4) * mm});
            skLineSegment(sketch, "E114", {"start": v(-66.68, 30.4) * mm, "end": v(-50.9, 30.4) * mm});
            skLineSegment(sketch, "E115", {"start": v(-8.1, 30.4) * mm, "end": v(-0.46, 30.4) * mm});
            skLineSegment(sketch, "E116", {"start": v(-0.46, 30.4) * mm, "end": v(-0.46, 27.4) * mm});
            skArc(sketch, "E117.trimOffspring", {"start": v(-8.1, 30.4) * mm, "mid": v(-29.5, 37.18) * mm, "end": v(-50.9, 30.4) * mm});
            skSolve(sketch);
        }
        {
            var Q0;
            Q0 = qSketchRegion(id + "F34", true);
            extrude(context, id + "F35", {"entities" : qUnion([Q0]), "oppositeDirection" : true, "depth" : 20 * mm, "offsetDistance" : 25 * mm});
        }
        {
            var Q0;
            Q0=qCreatedBy(id+"F29.planeOp",FACE);
            var sketch = newSketch(context, id + "F36", { "sketchPlane" : qUnion([Q0])});
            skLineSegment(sketch, "E118.bottom", {"start": v(-85.09, 63.9) * mm, "end": v(30.98, 63.9) * mm});
            skLineSegment(sketch, "E118.top", {"start": v(-85.09, 18.1) * mm, "end": v(30.98, 18.1) * mm});
            skLineSegment(sketch, "E118.left", {"start": v(-85.09, 63.9) * mm, "end": v(-85.09, 18.1) * mm});
            skLineSegment(sketch, "E118.right", {"start": v(30.98, 63.9) * mm, "end": v(30.98, 18.1) * mm});
            skSolve(sketch);
        }
        {
            var Q0;
            Q0=makeQuery(id+"F36.imprint","IMPRINT",FACE,{"disambiguationData":[TD([[makeQuery(id+"F36.imprint","IMPRINT",EDGE,{"derivedFrom":sQuery(id+"F36.wireOp",EDGE,"E118.bottom")}),-1.0]])]});
            var Q1;
            {var subQ0=sQuery(id+"F16.wireOp",EDGE,"E65");var subQ1=sQuery(id+"F8.wireOp",EDGE,"E39");var subQ2=sQuery(id+"F1.wireOp",EDGE,"E35");var subQ3=sQuery(id+"F1.wireOp",EDGE,"E31");var subQ4=makeQuery(id+"F9.opExtrude","SWEPT_FACE",FACE,{"disambiguationData":[OSD([subQ1])]});Q1=makeQuery(id+"F31.boolean.opBoolean","MERGE",FACE,{"derivedFrom":[makeQuery(id+"F23.boolean.opBoolean","MERGE",FACE,{"derivedFrom":[makeQuery(id+"F9.boolean.opBoolean","MERGE",FACE,{"derivedFrom":[makeQuery(id+"F2.opExtrude","SWEPT_FACE",FACE,{"disambiguationData":[OSD([subQ3])]}),subQ4]}),makeQuery(id+"F9.boolean.opBoolean","MERGE",FACE,{"derivedFrom":[makeQuery(id+"F2.opExtrude","SWEPT_FACE",FACE,{"disambiguationData":[OSD([subQ2])]}),subQ4]}),makeQuery(id+"F23.opExtrude","CAP_FACE",FACE,{"disambiguationData":[OSD([subQ0])],"isStart":true})]}),makeQuery(id+"F31.opExtrude","CAP_FACE",FACE,{"disambiguationData":[OSD([subQ3,subQ2,subQ1,subQ0])],"isStart":false})]});}
            extrude(context, id + "F37", {"entities" : qUnion([Q0]), "operationType" : NewBodyOperationType.REMOVE, "endBound" : BoundingType.UP_TO_SURFACE, "oppositeDirection" : true, "depth" : 25 * mm, "endBoundEntityFace" : qUnion([Q1]), "offsetDistance" : 25 * mm});
        }
        {
            var Q0;
            Q0=qCreatedBy(makeId("Front.planeOp"),FACE);
            var sketch = newSketch(context, id + "F38", { "sketchPlane" : qUnion([Q0])});
            skLineSegment(sketch, "E119.bottom", {"start": v(46.85, 22.98) * mm, "end": v(7.15, 22.98) * mm});
            skLineSegment(sketch, "E119.top", {"start": v(46.85, 0) * mm, "end": v(7.15, 0) * mm});
            skLineSegment(sketch, "E119.left", {"start": v(46.85, 22.98) * mm, "end": v(46.85, 0) * mm});
            skLineSegment(sketch, "E119.right", {"start": v(7.15, 22.98) * mm, "end": v(7.15, 0) * mm});
            skLineSegment(sketch, "E120.bottom", {"start": v(63.15, 22.1) * mm, "end": v(134.85, 22.1) * mm});
            skLineSegment(sketch, "E120.top", {"start": v(63.15, 0) * mm, "end": v(134.85, 0) * mm});
            skLineSegment(sketch, "E120.left", {"start": v(63.15, 22.1) * mm, "end": v(63.15, 0) * mm});
            skLineSegment(sketch, "E120.right", {"start": v(134.85, 22.1) * mm, "end": v(134.85, 0) * mm});
            skLineSegment(sketch, "E121.bottom", {"start": v(222.85, 21.32) * mm, "end": v(151.15, 21.32) * mm});
            skLineSegment(sketch, "E121.top", {"start": v(222.85, 0) * mm, "end": v(151.15, 0) * mm});
            skLineSegment(sketch, "E121.left", {"start": v(222.85, 21.32) * mm, "end": v(222.85, 0) * mm});
            skLineSegment(sketch, "E121.right", {"start": v(151.15, 21.32) * mm, "end": v(151.15, 0) * mm});
            skLineSegment(sketch, "E122.bottom", {"start": v(239.15, 20.56) * mm, "end": v(310.9, 20.56) * mm});
            skLineSegment(sketch, "E122.top", {"start": v(239.15, 0) * mm, "end": v(310.9, 0) * mm});
            skLineSegment(sketch, "E122.left", {"start": v(239.15, 20.56) * mm, "end": v(239.15, 0) * mm});
            skLineSegment(sketch, "E122.right", {"start": v(310.9, 20.56) * mm, "end": v(310.9, 0) * mm});
            skSolve(sketch);
        }
        {
            var Q0;
            Q0 = qSketchRegion(id + "F38", true);
            extrude(context, id + "F39", {"entities" : qUnion([Q0]), "operationType" : NewBodyOperationType.REMOVE, "endBound" : BoundingType.THROUGH_ALL, "oppositeDirection" : true, "depth" : 25 * mm, "offsetDistance" : 25 * mm, "hasSecondDirection" : true, "secondDirectionBound" : SecondDirectionBoundingType.THROUGH_ALL, "secondDirectionOppositeDirection" : false, "secondDirectionDepth" : 25 * mm});
        }
        {
            var Q0;
            {var subQ0=sQuery(id+"F8.wireOp",EDGE,"E41");Q0=makeQuery(id+"F39.boolean.opBoolean","SPLIT",FACE,{"disambiguationData":[TD([makeQuery(id+"F9.boolean.opBoolean","COPY",FACE,{"derivedFrom":makeQuery(id+"F9.opExtrude","SWEPT_FACE",FACE,{"disambiguationData":[OSD([subQ0])]})})])],"derivedFrom":makeQuery(id+"F37.boolean.opBoolean","COPY",FACE,{"derivedFrom":makeQuery(id+"F37.opExtrude","SWEPT_FACE",FACE,{"disambiguationData":[OSD([sQuery(id+"F36.wireOp",EDGE,"E118.top")])]})})});}
            var sketch = newSketch(context, id + "F40", { "sketchPlane" : qUnion([Q0])});
            skCircle(sketch, "E123", {"center": v(55, -12) * mm, "radius": 4 * mm});
            skCircle(sketch, "E124", {"center": v(143, -12) * mm, "radius": 4 * mm});
            skCircle(sketch, "E125", {"center": v(231, -12) * mm, "radius": 4 * mm});
            skCircle(sketch, "E126", {"center": v(319, -12) * mm, "radius": 4 * mm});
            skCircle(sketch, "E127", {"center": v(319, -47) * mm, "radius": 4 * mm});
            skCircle(sketch, "E128", {"center": v(231, -47) * mm, "radius": 4 * mm});
            skCircle(sketch, "E129", {"center": v(143, -47) * mm, "radius": 4 * mm});
            skCircle(sketch, "E130", {"center": v(55, -47) * mm, "radius": 4 * mm});
            skSolve(sketch);
        }
        {
            var Q0;
            Q0 = qSketchRegion(id + "F40", true);
            extrude(context, id + "F41", {"entities" : qUnion([Q0]), "operationType" : NewBodyOperationType.REMOVE, "oppositeDirection" : true, "depth" : 10.1 * mm, "offsetDistance" : 25 * mm});
        }
        {
            var Q0;
            Q0=qCreatedBy(id+"F14.planeOp",FACE);
            var sketch = newSketch(context, id + "F42", { "sketchPlane" : qUnion([Q0])});
            skCircle(sketch, "E131", {"center": v(0, -29.5) * mm, "radius": 10 * mm});
            skSolve(sketch);
        }
        {
            var Q0;
            Q0 = qSketchRegion(id + "F42", true);
            extrude(context, id + "F43", {"entities" : qUnion([Q0]), "operationType" : NewBodyOperationType.REMOVE, "oppositeDirection" : true, "depth" : 5 * mm, "offsetDistance" : 25 * mm});
        }
    });
